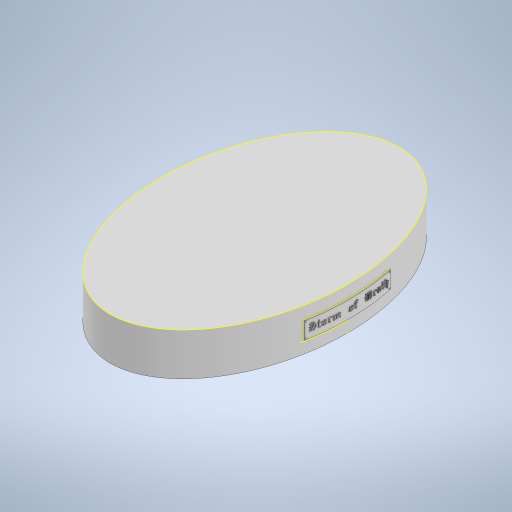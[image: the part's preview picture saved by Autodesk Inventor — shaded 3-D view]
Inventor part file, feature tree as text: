
AUTODESK INVENTOR PART (.ipt)
format: ipt  version: 2024 (Build 280153000, 153)  size: 3,596,288 bytes
history: native  units: mm
features: split x27, thicken_offset x17, sketch x4, extrude x2, plane x1, fillet x1, other x1
ambient origin geometry x8: Origin, YZ Plane, XZ Plane, XY Plane, X Axis, Y Axis, Z Axis, Center Point
bodies: Solid1 (feature_tree)
feature tree (53):
  extrude  "Extrusion1"  Depth=54.5mm
  extrude  "Extrusion2"  Depth=51.0mm
  plane  "Work Plane2"
  sketch  "Sketch4"  dims[d6=3.0mm d7=0.0mm d9=80.0mm d10=32.748225mm d14=10.0mm d16=51.0mm d19=0.75mm d20=0.75mm d21=0.75mm d22=0.75mm d23=0.75mm d25=0.75mm d26=0.75mm d27=0.75mm d28=0.75mm d70=0.75mm d71=0.75mm d72=0.5mm d73=0.5mm d74=0.5mm d75=0.5mm d76=0.5mm d77=0.5mm d78=0.5mm d79=0.5mm d80=0.5mm d81=0.5mm d82=0.5mm d83=0.5mm d84=0.5mm d85=0.5mm d86=0.5mm d87=0.5mm d88=0.5mm d89=0.5mm d90=0.5mm d91=0.5mm d92=0.5mm d93=0.5mm d94=0.5mm d95=0.5mm d96=0.4mm d97=0.4mm d98=0.4mm d99=0.4mm d100=0.4mm d101=0.4mm d102=0.4mm d103=0.4mm d104=0.35mm]
  sketch  "3D Sketch2"
  split  "Split28"
  split  "Split29"
  split  "Split30"
  split  "Split31"
  split  "Split32"
  split  "Split33"
  split  "Split34"
  split  "Split35"
  split  "Split36"
  split  "Split37"
  split  "Split38"
  split  "Split39"
  split  "Split40"
  split  "Split41"
  split  "Split42"
  split  "Split43"
  split  "Split44"
  split  "Split45"
  split  "Split46"
  split  "Split47"
  split  "Split48"
  split  "Split49"
  split  "Split50"
  split  "Split51"
  split  "Split52"
  split  "Split53"
  split  "Split54"
  thicken_offset  "Thicken20"
  thicken_offset  "Thicken21"
  thicken_offset  "Thicken22"
  thicken_offset  "Thicken23"
  thicken_offset  "Thicken24"
  thicken_offset  "Thicken25"
  thicken_offset  "Thicken26"
  thicken_offset  "Thicken27"
  thicken_offset  "Thicken28"
  thicken_offset  "Thicken29"
  thicken_offset  "Thicken30"
  thicken_offset  "Thicken31"
  thicken_offset  "Thicken32"
  thicken_offset  "Thicken33"
  thicken_offset  "Thicken34"
  thicken_offset  "Thicken35"
  thicken_offset  "Thicken36"
  fillet  "Fillet2"  Radius=22.0mm
  sketch  "Sketch1"  dims[d0=85.0mm d1=54.5mm]
  sketch  "Sketch2"  dims[d2=81.5mm d3=51.0mm d4=22.0mm d5=0.0mm]
  other  "Project to Surface2"
